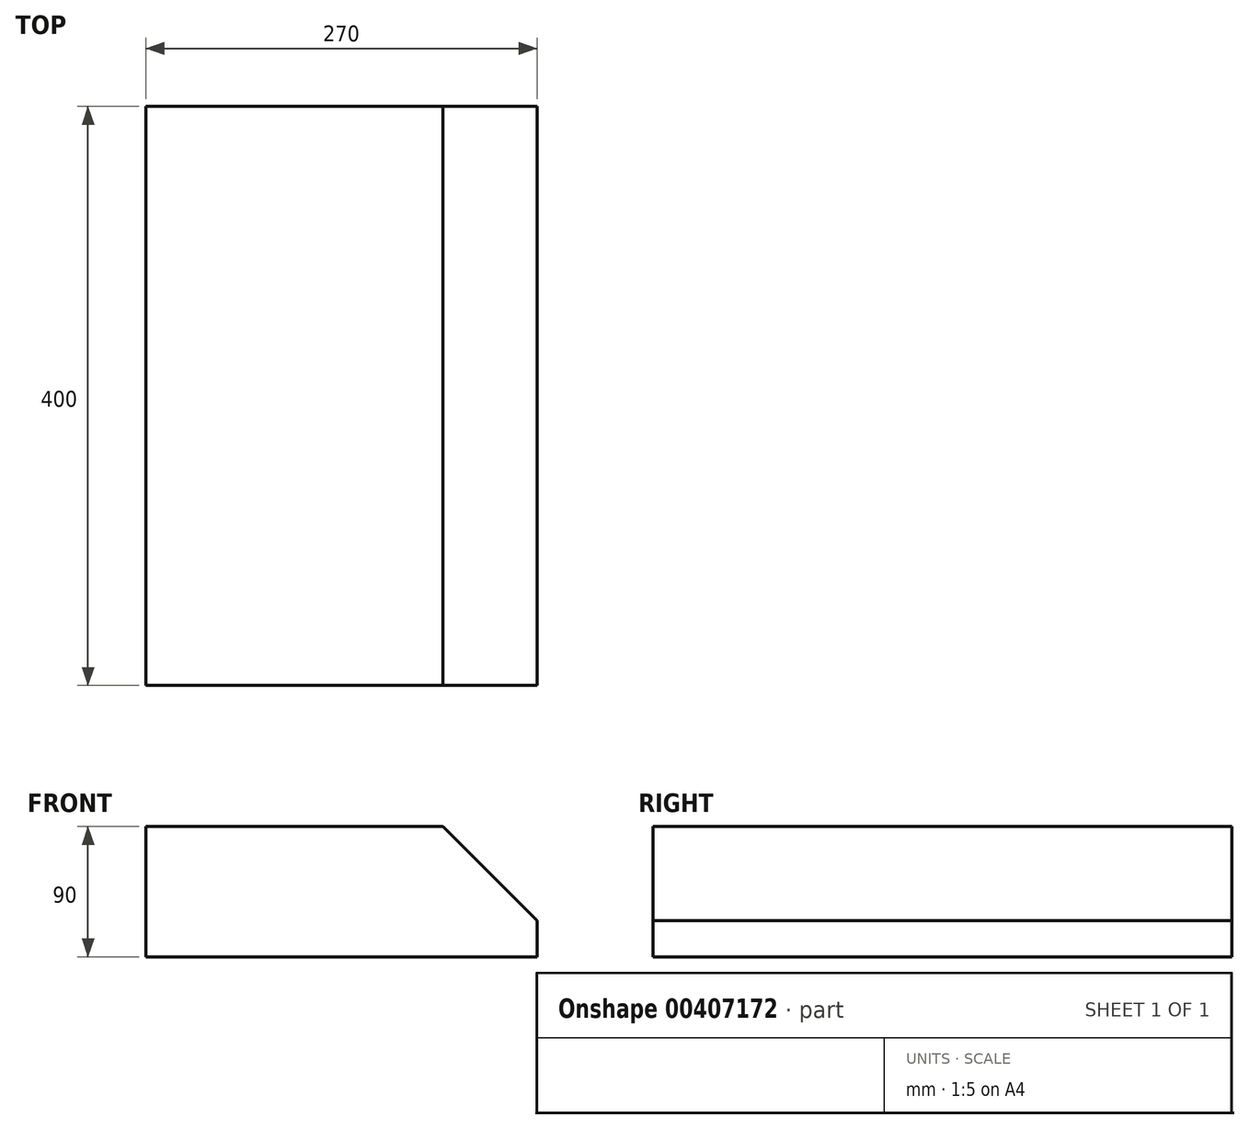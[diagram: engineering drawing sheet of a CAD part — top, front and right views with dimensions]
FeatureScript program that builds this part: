
annotation { "Feature Type Name" : "Feature", "Feature Type Description" : "" }
export const myFeature = defineFeature(function(context is Context, id is Id, definition is map)
    precondition{}
    {
        {
            var Q0;
            Q0=qCreatedBy(makeId("Front.planeOp"),FACE);
            var sketch = newSketch(context, id + "F0", { "sketchPlane" : qUnion([Q0])});
            skLineSegment(sketch, "E0.bottom", {"start": v(0, 0) * mm, "end": v(-270, 0) * mm});
            skLineSegment(sketch, "E0.top", {"start": v(-65, 90) * mm, "end": v(-270, 90) * mm});
            skLineSegment(sketch, "E0.left", {"start": v(0, 0) * mm, "end": v(0, 25) * mm});
            skLineSegment(sketch, "E0.right", {"start": v(-270, 0) * mm, "end": v(-270, 90) * mm});
            skLineSegment(sketch, "E1", {"start": v(0, 25) * mm, "end": v(-65, 90) * mm});
            skPoint(sketch, "E2.orphan", {"position": v(0, 90) * mm});
            skSolve(sketch);
        }
        {
            var Q0;
            Q0=makeQuery(id+"F0.imprint","IMPRINT",FACE,{"disambiguationData":[TD([[makeQuery(id+"F0.imprint","IMPRINT",EDGE,{"derivedFrom":sQuery(id+"F0.wireOp",EDGE,"E0.bottom")}),-1.0]])]});
            var Q1;
            Q1=makeQuery(id+"F0.imprint","IMPRINT",FACE,{"disambiguationData":[TD([[makeQuery(id+"F0.imprint","IMPRINT",EDGE,{"derivedFrom":sQuery(id+"F0.wireOp",EDGE,"2zq16BMh-DBYG-7P46-QInC-PGNC7a65GsiN.bottom")}),-1.0]])]});
            extrude(context, id + "F1", {"entities" : qUnion([Q0, Q1]), "depth" : 400 * mm, "offsetDistance" : 25 * mm});
        }
    });
